# Revit family: HALIMALED_31_3000MM_4000k
name_source: partatom
category: Lighting Fixtures
units: mm (PartAtom-declared; Revit-internal decimal feet)

## family parameters
Always vertical = Yes
Cut with Voids When Loaded = No
Host = Ceiling
Light Source = Yes
OmniClass Number = 23.80.70.11
OmniClass Title = Luminaries for Internal Lighting
Part Type = Normal
Room Calculation Point = No
Round Connector Dimension = Use Diameter
Shared = No

## types (1)
- Type 1
    Angle d'éclairage = 90°
    Color Filter = 16777215
    Default Elevation = 0 mm  [stored 0 ft]
    Diffuseur = Capot diffusant microprismatique
    Dimensions = 63x78 mm, L = 3000 mm
    Dimming Lamp Color Temperature Shift = <None>
    Driver = Driver Tridonic en version 230V on/off et Boke en DALI
    Durée de vie = 50 000 heures
    Emit from Line Length = 610 mm
    Fintion = Blanc
    IRC = >80
    Maintien du flux = L80B10 (50 000 heures)
    Matériau = Aluminium anodisé
    Photometric Web File = google_eulumdat_converter (3).ies
    Puissance nominale = 80W
    SDCM = <3
    Tension = AC 220-240V
    Tilt Angle = 90.00°
    Type = Profilé en saillie/suspension
    Type de lampe = LED Sanan

note: [stored X ft] marks values corroborated as IEEE doubles in the binary element streams (Revit-internal decimal feet)

## geometry (parser evidence)
native form markers: Sweep x2
no freeform markers — native parametric forms only
